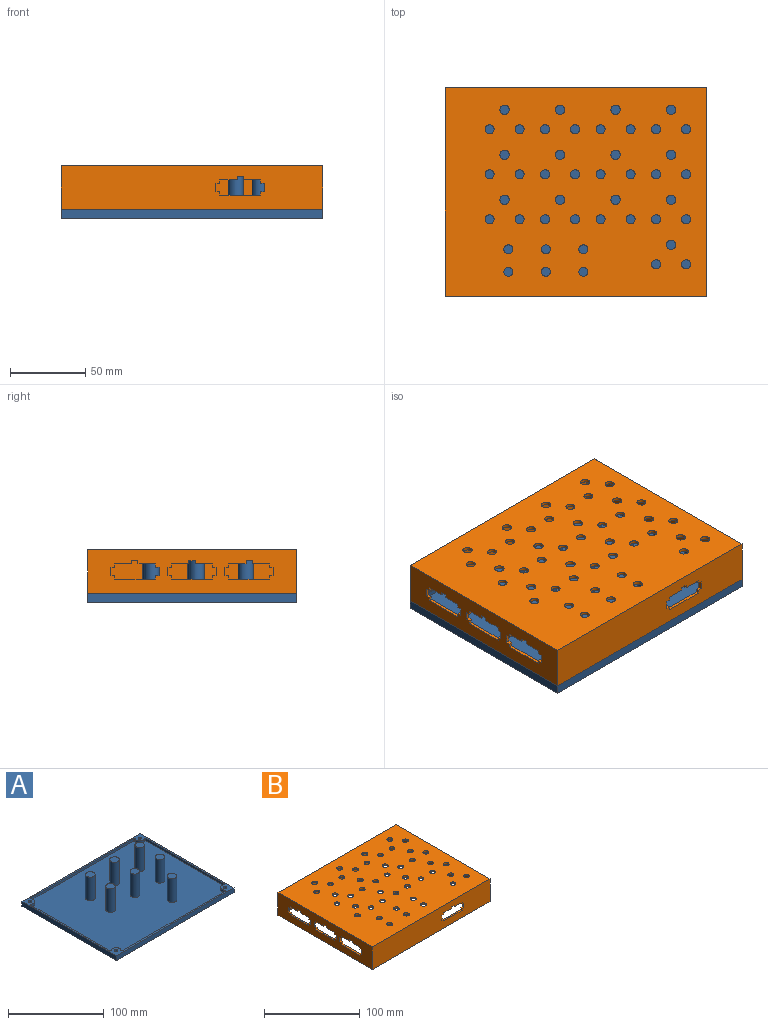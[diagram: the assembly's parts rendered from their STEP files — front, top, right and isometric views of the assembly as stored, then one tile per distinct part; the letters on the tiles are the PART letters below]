
ASSEMBLY  parts=2 mates=1
PART A: 51 faces, bbox 174.2x139x33 mm
  f0: plane 174x6mm, normal (0,-1,0), area 1044mm2, adj f1,f5,f6,f23
  f1: plane 137x6mm, normal (1,0,0), area 822mm2, adj f0,f2,f6,f23
  f2: plane 6x0.23mm, normal (0,-1,0), area 1.4mm2, adj f1,f3,f6,f23
  f3: plane 6x2mm, normal (1,0,0), area 12mm2, adj f2,f4,f6,f23
  f4: plane 174.23x6mm, normal (0,1,0), area 1045.4mm2, adj f3,f5,f6,f23
  f5: plane 139x6mm, normal (-1,0,0), area 834mm2, adj f0,f4,f6,f23
  f6: plane 174.23x139mm, normal (0,0,-1), area 24053.7mm2, adj f0,f1,f2,f3,f4,f5,f41,f44
  f7: cylinder r=1mm len=3mm, axis (0,0,-1), area 6.9mm2, adj f8,f22,f23,f38
  f8: plane 152.06x3mm, normal (0,1,0), area 456.2mm2, adj f7,f9,f23,f38
  f9: cylinder r=1mm len=3mm, axis (0,0,-1), area 6.9mm2, adj f8,f10,f23,f38
  f10: cylinder r=5mm len=8.33mm, axis (0,0,-1), area 45.5mm2, adj f9,f11,f23,f38
  f11: cylinder r=1mm len=3mm, axis (0,0,-1), area 6.9mm2, adj f10,f12,f23,f38
  f12: plane 116.33x3mm, normal (1,0,0), area 349mm2, adj f11,f13,f23,f38
  f13: cylinder r=1mm len=3mm, axis (0,0,-1), area 6.3mm2, adj f12,f14,f23,f38
  f14: cylinder r=5mm len=7.5mm, axis (0,0,-1), area 39.3mm2, adj f13,f15,f23,f38
  f15: cylinder r=1mm len=3mm, axis (0,0,-1), area 6.3mm2, adj f14,f16,f23,f38
  f16: plane 151.61x3mm, normal (0,-1,0), area 454.8mm2, adj f15,f17,f23,f38
  f17: cylinder r=1mm len=3mm, axis (0,0,-1), area 6.3mm2, adj f16,f18,f23,f38
  f18: cylinder r=5mm len=7.5mm, axis (0,0,-1), area 39.3mm2, adj f17,f19,f23,f38
  f19: cylinder r=1mm len=3mm, axis (0,0,-1), area 6.3mm2, adj f18,f20,f23,f38
  f20: plane 115.61x3mm, normal (-1,0,0), area 346.8mm2, adj f19,f21,f23,f38
  f21: cylinder r=1mm len=3mm, axis (0,0,-1), area 6.3mm2, adj f20,f22,f23,f38
  f22: cylinder r=5mm len=8.33mm, axis (0,0,-1), area 42.4mm2, adj f7,f21,f23,f38
  f23: plane 174.23x139mm, normal (0,0,1), area 1507.9mm2, adj f0,f1,f2,f3,f4,f5,f7,f8
  f24: plane 10x10mm, normal (0,0,1), area 78.5mm2, adj f31
  f25: plane 10x10mm, normal (0,0,1), area 78.5mm2, adj f32
  f26: plane 10x10mm, normal (0,0,1), area 78.5mm2, adj f33
  f27: plane 10x10mm, normal (0,0,1), area 78.5mm2, adj f34
  f28: plane 10x10mm, normal (0,0,1), area 78.5mm2, adj f35
  f29: plane 10x10mm, normal (0,0,1), area 78.5mm2, adj f36
  f30: plane 10x10mm, normal (0,0,1), area 78.5mm2, adj f37
  f31: cylinder r=5mm len=30mm, axis (0,0,-1), area 942.5mm2, adj f24,f38
  f32: cylinder r=5mm len=30mm, axis (0,0,-1), area 942.5mm2, adj f25,f38
  f33: cylinder r=5mm len=30mm, axis (0,0,-1), area 942.5mm2, adj f26,f38
  f34: cylinder r=5mm len=30mm, axis (0,0,-1), area 942.5mm2, adj f27,f38
  f35: cylinder r=5mm len=30mm, axis (0,0,-1), area 942.5mm2, adj f28,f38
  f36: cylinder r=5mm len=30mm, axis (0,0,-1), area 942.5mm2, adj f29,f38
  f37: cylinder r=5mm len=30mm, axis (0,0,-1), area 942.5mm2, adj f30,f38
  f38: plane 170x135mm, normal (0,0,1), area 22088.1mm2, adj f7,f8,f9,f10,f11,f12,f13,f14
  f39: cylinder r=1.8mm len=3.6mm, axis (0,0,-1), area 33.9mm2, adj f23,f40
  f40: plane 6.5x6.5mm, normal (0,0,-1), area 23mm2, adj f39,f41
  f41: cylinder r=3.25mm len=6.5mm, axis (0,0,-1), area 61.3mm2, adj f6,f40
  f42: cylinder r=1.8mm len=3.6mm, axis (0,0,-1), area 33.9mm2, adj f23,f43
  f43: plane 6.5x6.5mm, normal (0,0,-1), area 23mm2, adj f42,f44
  f44: cylinder r=3.25mm len=6.5mm, axis (0,0,-1), area 61.3mm2, adj f6,f43
  f45: cylinder r=1.8mm len=3.6mm, axis (0,0,-1), area 33.9mm2, adj f23,f46
  f46: plane 6.5x6.5mm, normal (0,0,-1), area 23mm2, adj f45,f47
  f47: cylinder r=3.25mm len=6.5mm, axis (0,0,-1), area 61.3mm2, adj f6,f46
  f48: cylinder r=1.8mm len=3.6mm, axis (0,0,-1), area 33.9mm2, adj f23,f49
  f49: plane 6.5x6.5mm, normal (0,0,-1), area 23mm2, adj f48,f50
  f50: cylinder r=3.25mm len=6.5mm, axis (0,0,-1), area 61.3mm2, adj f6,f49
PART B: 142 faces, bbox 174.2x139x29 mm
  f0: plane 139x29mm, normal (-1,0,0), area 3090.4mm2, adj f3,f7,f53,f69,f70,f71,f72,f73
  f1: plane 119x27mm, normal (1,0,0), area 2272.4mm2, adj f2,f58,f59,f69,f70,f71,f72,f73
  f2: plane 170x135mm, normal (0,0,-1), area 21426.1mm2, adj f1,f8,f9,f10,f11,f12,f13,f14
  f3: plane 174x29mm, normal (0,-1,0), area 4732.4mm2, adj f0,f4,f53,f69,f118,f119,f120,f121
  f4: plane 137x29mm, normal (1,0,0), area 3973mm2, adj f3,f5,f53,f69
  f5: plane 29x0.23mm, normal (0,-1,0), area 6.5mm2, adj f4,f6,f53,f69
  f6: plane 29x2mm, normal (1,0,0), area 58mm2, adj f5,f7,f53,f69
  f7: plane 174.23x29mm, normal (0,1,0), area 5052.5mm2, adj f0,f6,f53,f69
  f8: cylinder r=3mm len=6mm, axis (0,0,-1), area 37.7mm2, adj f2,f53
  f9: cylinder r=3mm len=6mm, axis (0,0,-1), area 37.7mm2, adj f2,f53
  f10: cylinder r=3mm len=6mm, axis (0,0,-1), area 37.7mm2, adj f2,f53
  f11: cylinder r=3mm len=6mm, axis (0,0,-1), area 37.7mm2, adj f2,f53
  f12: cylinder r=3mm len=6mm, axis (0,0,-1), area 37.7mm2, adj f2,f53
  f13: cylinder r=3mm len=6mm, axis (0,0,-1), area 37.7mm2, adj f2,f53
  f14: cylinder r=3.1mm len=6.2mm, axis (0,0,-1), area 39mm2, adj f2,f53
  f15: cylinder r=3mm len=6mm, axis (0,0,-1), area 37.7mm2, adj f2,f53
  f16: cylinder r=3mm len=6mm, axis (0,0,-1), area 37.7mm2, adj f2,f53
  f17: cylinder r=3.1mm len=6.2mm, axis (0,0,-1), area 39mm2, adj f2,f53
  f18: cylinder r=3.1mm len=6.2mm, axis (0,0,-1), area 39mm2, adj f2,f53
  f19: cylinder r=3.1mm len=6.2mm, axis (0,0,-1), area 39mm2, adj f2,f53
  f20: cylinder r=3.1mm len=6.2mm, axis (0,0,-1), area 39mm2, adj f2,f53
  f21: cylinder r=3mm len=6mm, axis (0,0,-1), area 37.7mm2, adj f2,f53
  f22: cylinder r=3mm len=6mm, axis (0,0,-1), area 37.7mm2, adj f2,f53
  f23: cylinder r=3mm len=6mm, axis (0,0,-1), area 37.7mm2, adj f2,f53
  f24: cylinder r=3mm len=6mm, axis (0,0,-1), area 37.7mm2, adj f2,f53
  f25: cylinder r=3mm len=6mm, axis (0,0,-1), area 37.7mm2, adj f2,f53
  f26: cylinder r=3mm len=6mm, axis (0,0,-1), area 37.7mm2, adj f2,f53
  f27: cylinder r=3mm len=6mm, axis (0,0,-1), area 37.7mm2, adj f2,f53
  f28: cylinder r=3mm len=6mm, axis (0,0,-1), area 37.7mm2, adj f2,f53
  f29: cylinder r=3.1mm len=6.2mm, axis (0,0,-1), area 39mm2, adj f2,f53
  f30: cylinder r=3.1mm len=6.2mm, axis (0,0,-1), area 39mm2, adj f2,f53
  f31: cylinder r=3.1mm len=6.2mm, axis (0,0,-1), area 39mm2, adj f2,f53
  f32: cylinder r=3.1mm len=6.2mm, axis (0,0,-1), area 39mm2, adj f2,f53
  f33: cylinder r=3mm len=6mm, axis (0,0,-1), area 37.7mm2, adj f2,f53
  f34: cylinder r=3mm len=6mm, axis (0,0,-1), area 37.7mm2, adj f2,f53
  f35: cylinder r=3mm len=6mm, axis (0,0,-1), area 37.7mm2, adj f2,f53
  f36: cylinder r=3mm len=6mm, axis (0,0,-1), area 37.7mm2, adj f2,f53
  f37: cylinder r=3mm len=6mm, axis (0,0,-1), area 37.7mm2, adj f2,f53
  f38: cylinder r=3mm len=6mm, axis (0,0,-1), area 37.7mm2, adj f2,f53
  f39: cylinder r=3mm len=6mm, axis (0,0,-1), area 37.7mm2, adj f2,f53
  f40: cylinder r=3mm len=6mm, axis (0,0,-1), area 37.7mm2, adj f2,f53
  f41: cylinder r=3mm len=6mm, axis (0,0,-1), area 37.7mm2, adj f2,f53
  f42: cylinder r=3.1mm len=6.2mm, axis (0,0,-1), area 39mm2, adj f2,f53
  f43: cylinder r=3mm len=6mm, axis (0,0,-1), area 37.7mm2, adj f2,f53
  f44: cylinder r=3mm len=6mm, axis (0,0,-1), area 37.7mm2, adj f2,f53
  f45: cylinder r=3.1mm len=6.2mm, axis (0,0,-1), area 39mm2, adj f2,f53
  f46: cylinder r=3mm len=6mm, axis (0,0,-1), area 37.7mm2, adj f2,f53
  f47: cylinder r=3mm len=6mm, axis (0,0,-1), area 37.7mm2, adj f2,f53
  f48: cylinder r=3.1mm len=6.2mm, axis (0,0,-1), area 39mm2, adj f2,f53
  f49: cylinder r=3mm len=6mm, axis (0,0,-1), area 37.7mm2, adj f2,f53
  f50: cylinder r=3.1mm len=6.2mm, axis (0,0,-1), area 39mm2, adj f2,f53
  f51: cylinder r=3mm len=6mm, axis (0,0,-1), area 37.7mm2, adj f2,f53
  f52: cylinder r=3mm len=6mm, axis (0,0,-1), area 37.7mm2, adj f2,f53
  f53: plane 174.23x139mm, normal (0,0,1), area 22889.2mm2, adj f0,f3,f4,f5,f6,f7,f8,f9
  f54: cylinder r=1mm len=27mm, axis (0,0,1), area 59.8mm2, adj f2,f55,f68,f69
  f55: plane 154x27mm, normal (0,1,0), area 3844.4mm2, adj f2,f54,f56,f69,f118,f119,f120,f121
  f56: cylinder r=1mm len=27mm, axis (0,0,1), area 59.8mm2, adj f2,f55,f57,f69
  f57: cylinder r=4mm len=27mm, axis (0,0,1), area 308.6mm2, adj f2,f56,f58,f69
  f58: cylinder r=1mm len=27mm, axis (0,0,1), area 59.8mm2, adj f1,f2,f57,f69
  f59: cylinder r=1mm len=27mm, axis (0,0,1), area 59.8mm2, adj f1,f2,f60,f69
  f60: cylinder r=4mm len=27mm, axis (0,0,1), area 308.6mm2, adj f2,f59,f61,f69
  f61: cylinder r=1mm len=27mm, axis (0,0,1), area 59.8mm2, adj f2,f60,f62,f69
  f62: plane 154x27mm, normal (0,-1,0), area 4158mm2, adj f2,f61,f63,f69
  f63: cylinder r=1mm len=27mm, axis (0,0,1), area 59.8mm2, adj f2,f62,f64,f69
  f64: cylinder r=4mm len=27mm, axis (0,0,1), area 308.6mm2, adj f2,f63,f65,f69
  f65: cylinder r=1mm len=27mm, axis (0,0,1), area 59.8mm2, adj f2,f64,f66,f69
  f66: plane 119x27mm, normal (-1,0,0), area 3213mm2, adj f2,f65,f67,f69
  f67: cylinder r=1mm len=27mm, axis (0,0,1), area 59.8mm2, adj f2,f66,f68,f69
  f68: cylinder r=4mm len=27mm, axis (0,0,1), area 308.6mm2, adj f2,f54,f67,f69
  f69: plane 174.23x139mm, normal (0,0,-1), area 1384.5mm2, adj f0,f1,f3,f4,f5,f6,f7,f54
  f70: plane 2x2mm, normal (0,1,0), area 4mm2, adj f0,f1,f71,f85
  f71: plane 4x2mm, normal (0,0,-1), area 8mm2, adj f0,f1,f70,f72
  f72: plane 2x2mm, normal (0,-1,0), area 4mm2, adj f0,f1,f71,f73
  f73: plane 11.55x2mm, normal (0,0,-1), area 23.1mm2, adj f0,f1,f72,f74
  f74: plane 2.35x2mm, normal (0,-1,0), area 4.7mm2, adj f0,f1,f73,f75
  f75: plane 2.64x2mm, normal (0,0,-1), area 5.3mm2, adj f0,f1,f74,f76
  f76: plane 5.5x2mm, normal (0,-1,0), area 11mm2, adj f0,f1,f75,f77
  f77: plane 2.65x2mm, normal (0,0,1), area 5.3mm2, adj f0,f1,f76,f78
  f78: plane 2.35x2mm, normal (0,-1,0), area 4.7mm2, adj f0,f1,f77,f79
  f79: plane 27.1x2mm, normal (0,0,1), area 54.2mm2, adj f0,f1,f78,f80
  f80: plane 2.35x2mm, normal (0,1,0), area 4.7mm2, adj f0,f1,f79,f81
  f81: plane 2.65x2mm, normal (0,0,1), area 5.3mm2, adj f0,f1,f80,f82
  f82: plane 5.5x2mm, normal (0,1,0), area 11mm2, adj f0,f1,f81,f83
  f83: plane 2.65x2mm, normal (0,0,-1), area 5.3mm2, adj f0,f1,f82,f84
  f84: plane 2.35x2mm, normal (0,1,0), area 4.7mm2, adj f0,f1,f83,f85
  f85: plane 11.55x2mm, normal (0,0,-1), area 23.1mm2, adj f0,f1,f70,f84
  f86: plane 2x2mm, normal (0,1,0), area 4mm2, adj f0,f1,f87,f101
  f87: plane 4x2mm, normal (0,0,-1), area 8mm2, adj f0,f1,f86,f88
  f88: plane 2x2mm, normal (0,-1,0), area 4mm2, adj f0,f1,f87,f89
  f89: plane 11.55x2mm, normal (0,0,-1), area 23.1mm2, adj f0,f1,f88,f90
  f90: plane 2.35x2mm, normal (0,-1,0), area 4.7mm2, adj f0,f1,f89,f91
  f91: plane 2.64x2mm, normal (0,0,-1), area 5.3mm2, adj f0,f1,f90,f92
  f92: plane 5.5x2mm, normal (0,-1,0), area 11mm2, adj f0,f1,f91,f93
  f93: plane 2.65x2mm, normal (0,0,1), area 5.3mm2, adj f0,f1,f92,f94
  f94: plane 2.35x2mm, normal (0,-1,0), area 4.7mm2, adj f0,f1,f93,f95
  f95: plane 27.1x2mm, normal (0,0,1), area 54.2mm2, adj f0,f1,f94,f96
  f96: plane 2.35x2mm, normal (0,1,0), area 4.7mm2, adj f0,f1,f95,f97
  f97: plane 2.65x2mm, normal (0,0,1), area 5.3mm2, adj f0,f1,f96,f98
  f98: plane 5.5x2mm, normal (0,1,0), area 11mm2, adj f0,f1,f97,f99
  f99: plane 2.65x2mm, normal (0,0,-1), area 5.3mm2, adj f0,f1,f98,f100
  f100: plane 2.35x2mm, normal (0,1,0), area 4.7mm2, adj f0,f1,f99,f101
  f101: plane 11.55x2mm, normal (0,0,-1), area 23.1mm2, adj f0,f1,f86,f100
  f102: plane 2.65x2mm, normal (0,0,1), area 5.3mm2, adj f0,f1,f103,f117
  f103: plane 5.5x2mm, normal (0,1,0), area 11mm2, adj f0,f1,f102,f104
  f104: plane 2.65x2mm, normal (0,0,-1), area 5.3mm2, adj f0,f1,f103,f105
  f105: plane 2.35x2mm, normal (0,1,0), area 4.7mm2, adj f0,f1,f104,f106
  f106: plane 11.55x2mm, normal (0,0,-1), area 23.1mm2, adj f0,f1,f105,f107
  f107: plane 2x2mm, normal (0,1,0), area 4mm2, adj f0,f1,f106,f108
  f108: plane 4x2mm, normal (0,0,-1), area 8mm2, adj f0,f1,f107,f109
  f109: plane 2x2mm, normal (0,-1,0), area 4mm2, adj f0,f1,f108,f110
  f110: plane 11.55x2mm, normal (0,0,-1), area 23.1mm2, adj f0,f1,f109,f111
  f111: plane 2.35x2mm, normal (0,-1,0), area 4.7mm2, adj f0,f1,f110,f112
  f112: plane 2.64x2mm, normal (0,0,-1), area 5.3mm2, adj f0,f1,f111,f113
  f113: plane 5.5x2mm, normal (0,-1,0), area 11mm2, adj f0,f1,f112,f114
  f114: plane 2.65x2mm, normal (0,0,1), area 5.3mm2, adj f0,f1,f113,f115
  f115: plane 2.35x2mm, normal (0,-1,0), area 4.7mm2, adj f0,f1,f114,f116
  f116: plane 27.1x2mm, normal (0,0,1), area 54.2mm2, adj f0,f1,f115,f117
  f117: plane 2.35x2mm, normal (0,1,0), area 4.7mm2, adj f0,f1,f102,f116
  f118: plane 2.35x2mm, normal (-1,0,0), area 4.7mm2, adj f3,f55,f119,f133
  f119: plane 2.65x2mm, normal (0,0,1), area 5.3mm2, adj f3,f55,f118,f120
  f120: plane 5.5x2mm, normal (-1,0,0), area 11mm2, adj f3,f55,f119,f121
  f121: plane 2.65x2mm, normal (0,0,-1), area 5.3mm2, adj f3,f55,f120,f122
  f122: plane 2.35x2mm, normal (-1,0,0), area 4.7mm2, adj f3,f55,f121,f123
  f123: plane 11.55x2mm, normal (0,0,-1), area 23.1mm2, adj f3,f55,f122,f124
  f124: plane 2x2mm, normal (-1,0,0), area 4mm2, adj f3,f55,f123,f125
  f125: plane 4x2mm, normal (0,0,-1), area 8mm2, adj f3,f55,f124,f126
  f126: plane 2x2mm, normal (1,0,0), area 4mm2, adj f3,f55,f125,f127
  f127: plane 11.55x2mm, normal (0,0,-1), area 23.1mm2, adj f3,f55,f126,f128
  f128: plane 2.35x2mm, normal (1,0,0), area 4.7mm2, adj f3,f55,f127,f129
  f129: plane 2.65x2mm, normal (0,0,-1), area 5.3mm2, adj f3,f55,f128,f130
  f130: plane 5.5x2mm, normal (1,0,0), area 11mm2, adj f3,f55,f129,f131
  f131: plane 2.65x2mm, normal (0,0,1), area 5.3mm2, adj f3,f55,f130,f132
  f132: plane 2.35x2mm, normal (1,0,0), area 4.7mm2, adj f3,f55,f131,f133
  f133: plane 27.1x2mm, normal (0,0,1), area 54.2mm2, adj f3,f55,f118,f132
  f134: cone r=0mm half-angle=59deg, axis (0,0,-1), area 22.9mm2, adj f135
  f135: cylinder r=2.5mm len=20mm, axis (0,0,-1), area 314.2mm2, adj f69,f134
  f136: cone r=0mm half-angle=59deg, axis (0,0,-1), area 22.9mm2, adj f137
  f137: cylinder r=2.5mm len=20mm, axis (0,0,-1), area 314.2mm2, adj f69,f136
  f138: cone r=0mm half-angle=59deg, axis (0,0,-1), area 22.9mm2, adj f139
  f139: cylinder r=2.5mm len=20mm, axis (0,0,-1), area 314.2mm2, adj f69,f138
  f140: cone r=0mm half-angle=59deg, axis (0,0,-1), area 22.9mm2, adj f141
  f141: cylinder r=2.5mm len=20mm, axis (0,0,-1), area 314.2mm2, adj f69,f140
PLACE A t=(-209,0,-33)mm
PLACE B t=(-209,-1,0)mm
MATE fastened A.f23 <-> B.f69  axis (0,0,1) through (-308.85,68.39,-27)mm
